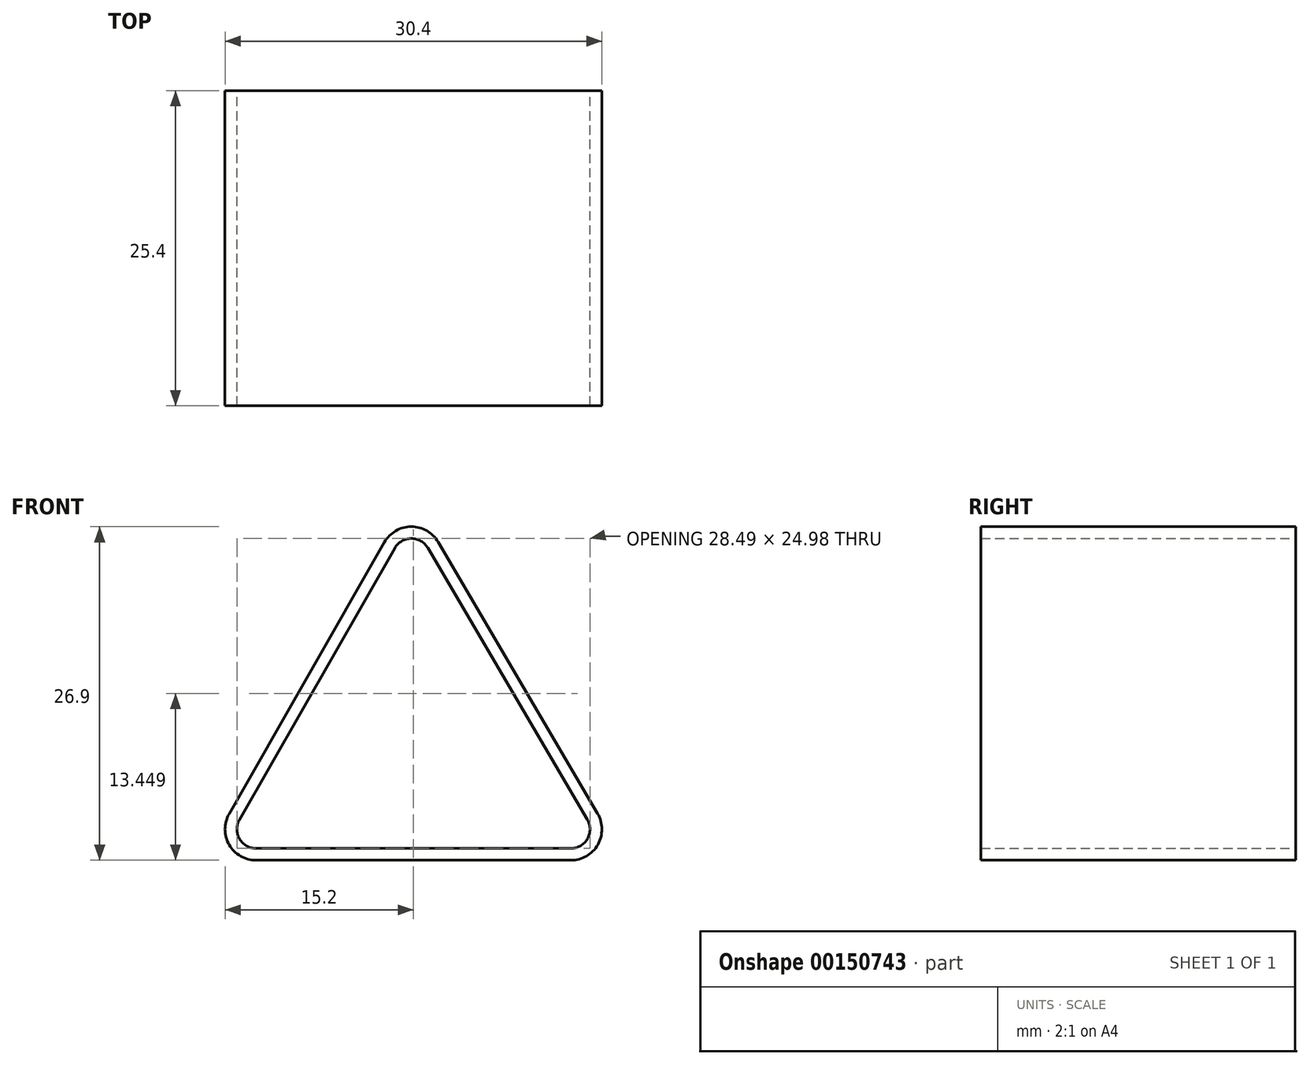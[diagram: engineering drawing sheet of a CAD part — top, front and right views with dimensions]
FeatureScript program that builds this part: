
annotation { "Feature Type Name" : "Feature", "Feature Type Description" : "" }
export const myFeature = defineFeature(function(context is Context, id is Id, definition is map)
    precondition{}
    {
        {
            var Q0;
            Q0=qCreatedBy(makeId("Front.planeOp"),FACE);
            var sketch = newSketch(context, id + "F0", { "sketchPlane" : qUnion([Q0])});
            skArc(sketch, "E0", {"start": v(2.16, 23.17) * mm, "mid": v(-0.01, 24.4) * mm, "end": v(-2.17, 23.14) * mm});
            skArc(sketch, "E1", {"start": v(-14.7, 1.24) * mm, "mid": v(-14.7, -1.26) * mm, "end": v(-12.53, -2.5) * mm});
            skArc(sketch, "E2", {"start": v(12.87, -2.5) * mm, "mid": v(15.04, -1.24) * mm, "end": v(15.03, 1.27) * mm});
            skLineSegment(sketch, "E3", {"start": v(-12.53, -2.5) * mm, "end": v(12.87, -2.5) * mm});
            skLineSegment(sketch, "E4", {"start": v(15.03, 1.27) * mm, "end": v(2.16, 23.17) * mm});
            skLineSegment(sketch, "E5", {"start": v(-14.7, 1.24) * mm, "end": v(-2.17, 23.14) * mm});
            skArc(sketch, "E6", {"start": v(1.33, 22.68) * mm, "mid": v(0, 23.44) * mm, "end": v(-1.34, 22.66) * mm});
            skArc(sketch, "E7", {"start": v(-13.87, 0.77) * mm, "mid": v(-13.86, -0.77) * mm, "end": v(-12.53, -1.54) * mm});
            skArc(sketch, "E8", {"start": v(12.87, -1.54) * mm, "mid": v(14.2, -0.77) * mm, "end": v(14.2, 0.78) * mm});
            skLineSegment(sketch, "E9", {"start": v(-13.87, 0.77) * mm, "end": v(-1.34, 22.66) * mm});
            skLineSegment(sketch, "E10", {"start": v(1.33, 22.68) * mm, "end": v(14.2, 0.78) * mm});
            skLineSegment(sketch, "E11", {"start": v(12.87, -1.54) * mm, "end": v(-12.53, -1.54) * mm});
            skSolve(sketch);
        }
        {
            var Q0;
            Q0=makeQuery(id+"F0.imprint","IMPRINT",FACE,{"disambiguationData":[TD([[makeQuery(id+"F0.imprint","IMPRINT",EDGE,{"derivedFrom":sQuery(id+"F0.wireOp",EDGE,"E0")}),1.0]])]});
            extrude(context, id + "F1", {"entities" : qUnion([Q0]), "depth" : 25.4 * mm});
        }
    });
